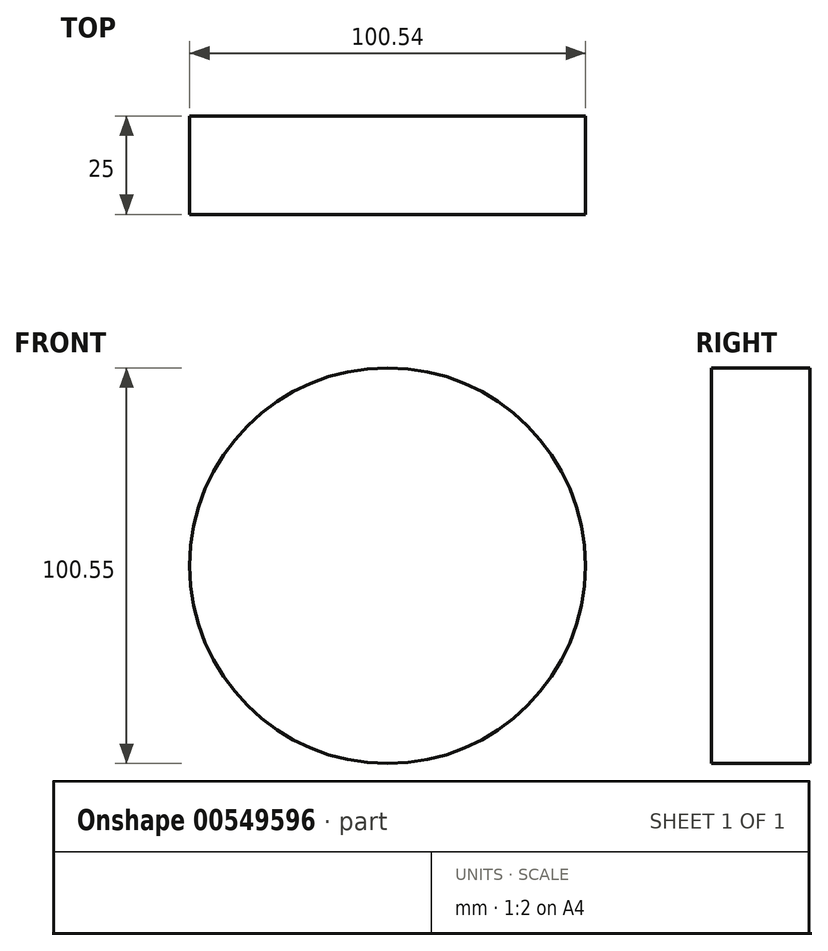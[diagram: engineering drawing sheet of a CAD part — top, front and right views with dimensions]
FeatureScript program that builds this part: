
annotation { "Feature Type Name" : "Feature", "Feature Type Description" : "" }
export const myFeature = defineFeature(function(context is Context, id is Id, definition is map)
    precondition{}
    {
        {
            var Q0;
            Q0=qCreatedBy(makeId("Front.planeOp"),FACE);
            var sketch = newSketch(context, id + "F0", { "sketchPlane" : qUnion([Q0])});
            skCircle(sketch, "E0", {"center": v(-158.7, -41.6) * mm, "radius": 50.27 * mm});
            skSolve(sketch);
        }
        {
            var Q0;
            Q0 = qSketchRegion(id + "F0", true);
            extrude(context, id + "F1", {"entities" : qUnion([Q0]), "depth" : 25 * mm, "offsetDistance" : 25 * mm});
        }
    });
